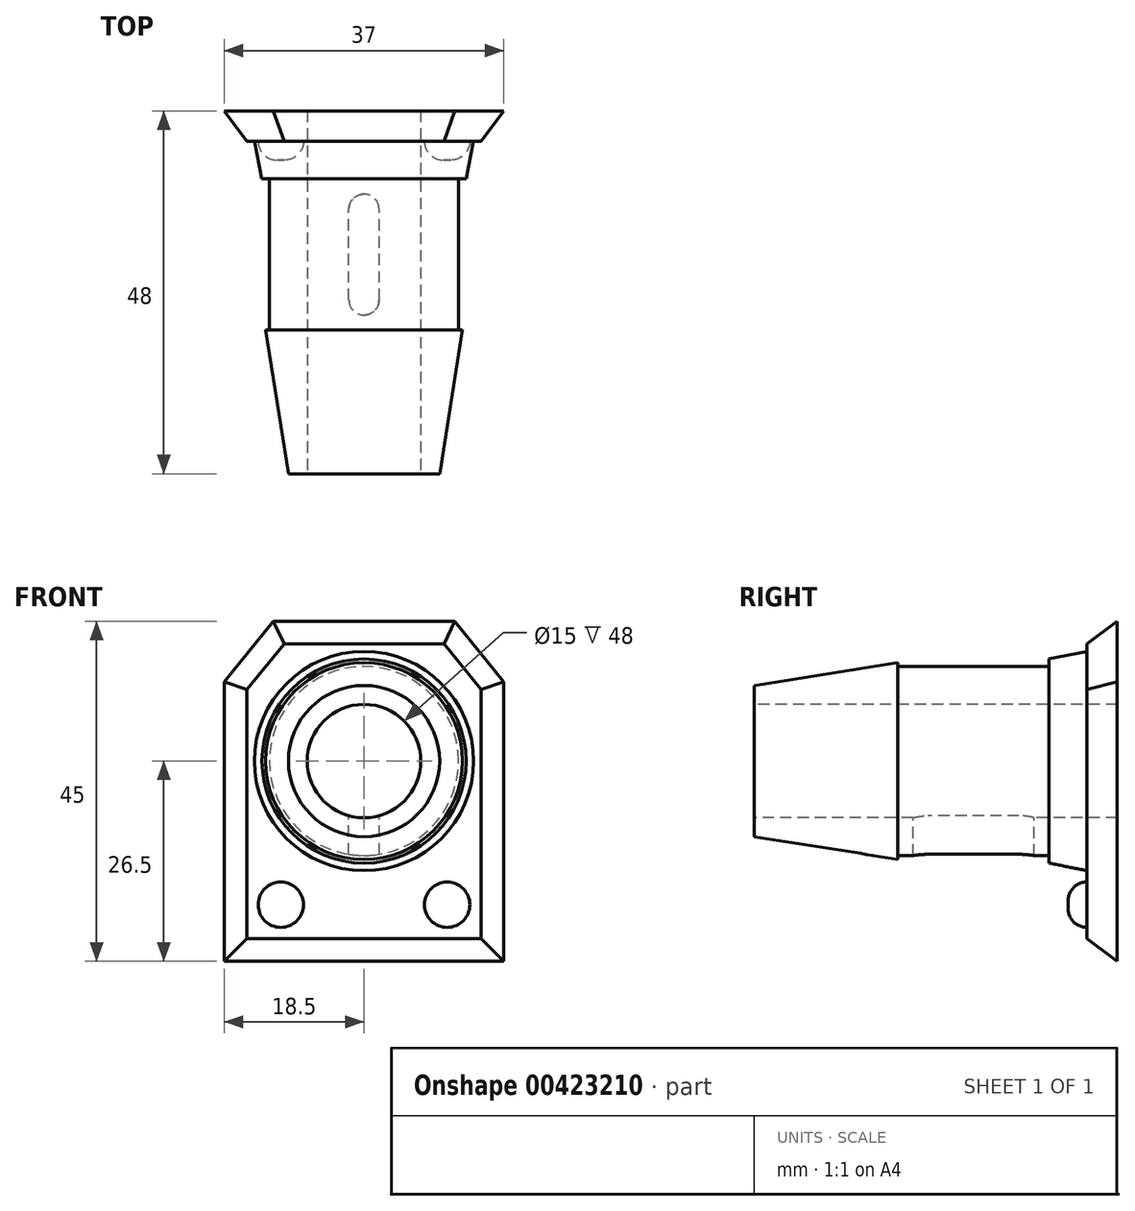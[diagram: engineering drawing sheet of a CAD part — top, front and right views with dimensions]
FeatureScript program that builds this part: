
annotation { "Feature Type Name" : "Feature", "Feature Type Description" : "" }
export const myFeature = defineFeature(function(context is Context, id is Id, definition is map)
    precondition{}
    {
        {
            var Q0;
            Q0=qCreatedBy(makeId("Front.planeOp"),FACE);
            var sketch = newSketch(context, id + "F0", { "sketchPlane" : qUnion([Q0])});
            skLineSegment(sketch, "E0.bottom", {"start": v(-18.5, 22.5) * mm, "end": v(18.5, 22.5) * mm});
            skLineSegment(sketch, "E0.top", {"start": v(-18.5, -22.5) * mm, "end": v(18.5, -22.5) * mm});
            skLineSegment(sketch, "E0.left", {"start": v(-18.5, 22.5) * mm, "end": v(-18.5, -22.5) * mm});
            skLineSegment(sketch, "E0.right", {"start": v(18.5, 22.5) * mm, "end": v(18.5, -22.5) * mm});
            skLineSegment(sketch, "E1", {"start": v(-18.5, 0) * mm, "end": v(18.5, 0) * mm});
            skPoint(sketch, "E2", {"position": v(0, 0) * mm});
            skSolve(sketch);
        }
        {
            var Q0;
            Q0=makeQuery(id+"F0.imprint","IMPRINT",FACE,{"disambiguationData":[TD([[makeQuery(id+"F0.imprint","IMPRINT",EDGE,{"derivedFrom":sQuery(id+"F0.wireOp",EDGE,"E0.bottom")}),-1.0]])]});
            var Q1;
            {var subQ0=sQuery(id+"F0.wireOp",EDGE,"E0.top");Q1=makeQuery(id+"F0.imprint","IMPRINT",FACE,{"disambiguationData":[TD([[makeQuery(id+"F0.imprint","IMPRINT",EDGE,{"derivedFrom":subQ0}),1.0]])]});}
            extrude(context, id + "F1", {"entities" : qUnion([Q0, Q1]), "depth" : 4 * mm});
        }
        {
            var Q0;
            Q0=makeQuery(id+"F1.opExtrude","SWEPT_EDGE",EDGE,{"disambiguationData":[OSD([sQuery(id+"F0.wireOp",EDGE,"E0.bottom"),sQuery(id+"F0.wireOp",EDGE,"E0.left")])]});
            var Q1;
            Q1=makeQuery(id+"F1.opExtrude","SWEPT_EDGE",EDGE,{"disambiguationData":[OSD([sQuery(id+"F0.wireOp",EDGE,"E0.bottom"),sQuery(id+"F0.wireOp",EDGE,"E0.right")])]});
            chamfer(context, id + "F2", {"entities" : qUnion([Q0, Q1]), "chamferType" : ChamferType.TWO_OFFSETS, "width1" : 8 * mm, "oppositeDirection" : false, "width2" : 6.5 * mm, "tangentPropagation" : true});
        }
        {
            var Q0;
            Q0=makeQuery(id+"F1.opExtrude","CAP_EDGE",EDGE,{"disambiguationData":[OSD([sQuery(id+"F0.wireOp",EDGE,"E0.left")])],"isStart":false});
            var Q1;
            Q1=makeQuery(id+"F1.opExtrude","CAP_EDGE",EDGE,{"disambiguationData":[OSD([sQuery(id+"F0.wireOp",EDGE,"E0.top")])],"isStart":false});
            var Q2;
            Q2=makeQuery(id+"F1.opExtrude","CAP_EDGE",EDGE,{"disambiguationData":[OSD([sQuery(id+"F0.wireOp",EDGE,"E0.right")])],"isStart":false});
            var Q3;
            {var subQ0=sQuery(id+"F0.wireOp",EDGE,"E0.right");var subQ1=sQuery(id+"F0.wireOp",EDGE,"E0.bottom");Q3=makeQuery(id+"F2.opChamfer","BLEND_EDGE",EDGE,{"blendedFrom":[makeQuery(id+"F1.opExtrude","SWEPT_EDGE",EDGE,{"disambiguationData":[OSD([subQ1,subQ0])]}),makeQuery(id+"F1.opExtrude","CAP_FACE",FACE,{"disambiguationData":[OSD([subQ1,sQuery(id+"F0.wireOp",EDGE,"E0.top"),sQuery(id+"F0.wireOp",EDGE,"E0.left"),subQ0])],"isStart":false})],"blendedInto":[makeQuery(id+"F1.opExtrude","CAP_FACE",FACE,{"disambiguationData":[OSD([subQ1,sQuery(id+"F0.wireOp",EDGE,"E0.top"),sQuery(id+"F0.wireOp",EDGE,"E0.left"),subQ0])],"isStart":false})]});}
            var Q4;
            {var subQ0=sQuery(id+"F0.wireOp",EDGE,"E0.left");var subQ1=sQuery(id+"F0.wireOp",EDGE,"E0.bottom");Q4=makeQuery(id+"F2.opChamfer","BLEND_EDGE",EDGE,{"blendedFrom":[makeQuery(id+"F1.opExtrude","SWEPT_EDGE",EDGE,{"disambiguationData":[OSD([subQ1,subQ0])]}),makeQuery(id+"F1.opExtrude","CAP_FACE",FACE,{"disambiguationData":[OSD([subQ1,sQuery(id+"F0.wireOp",EDGE,"E0.top"),subQ0,sQuery(id+"F0.wireOp",EDGE,"E0.right")])],"isStart":false})],"blendedInto":[makeQuery(id+"F1.opExtrude","CAP_FACE",FACE,{"disambiguationData":[OSD([subQ1,sQuery(id+"F0.wireOp",EDGE,"E0.top"),subQ0,sQuery(id+"F0.wireOp",EDGE,"E0.right")])],"isStart":false})]});}
            var Q5;
            Q5=makeQuery(id+"F1.opExtrude","CAP_EDGE",EDGE,{"disambiguationData":[OSD([sQuery(id+"F0.wireOp",EDGE,"E0.bottom")])],"isStart":false});
            chamfer(context, id + "F3", {"entities" : qUnion([Q0, Q1, Q2, Q3, Q4, Q5]), "chamferType" : ChamferType.TWO_OFFSETS, "width1" : 3 * mm, "oppositeDirection" : false, "width2" : 4 * mm, "tangentPropagation" : true});
        }
        {
            var Q0;
            Q0=makeQuery(id+"F1.opExtrude","CAP_FACE",FACE,{"disambiguationData":[OSD([sQuery(id+"F0.wireOp",EDGE,"E0.bottom"),sQuery(id+"F0.wireOp",EDGE,"E0.top"),sQuery(id+"F0.wireOp",EDGE,"E0.left"),sQuery(id+"F0.wireOp",EDGE,"E0.right")])],"isStart":false});
            var sketch = newSketch(context, id + "F4", { "sketchPlane" : qUnion([Q0])});
            skLineSegment(sketch, "E3", {"start": v(0, 19.5) * mm, "end": v(0, 4) * mm});
            skCircle(sketch, "E4", {"center": v(0, 4) * mm, "radius": 14.5 * mm});
            skSolve(sketch);
        }
        {
            var Q0;
            Q0=makeQuery(id+"F4.imprint","IMPRINT",FACE,{"disambiguationData":[TD([[makeQuery(id+"F4.imprint","IMPRINT",EDGE,{"derivedFrom":sQuery(id+"F4.wireOp",EDGE,"E4")}),1.0]])]});
            extrude(context, id + "F5", {"entities" : qUnion([Q0]), "operationType" : NewBodyOperationType.ADD, "depth" : 5 * mm});
        }
        {
            var Q0;
            Q0=makeQuery(id+"F5.opExtrude","CAP_FACE",FACE,{"disambiguationData":[OSD([sQuery(id+"F4.wireOp",EDGE,"E4")])],"isStart":false});
            var sketch = newSketch(context, id + "F6", { "sketchPlane" : qUnion([Q0])});
            skCircle(sketch, "E5", {"center": v(0, 4) * mm, "radius": 12.5 * mm});
            skSolve(sketch);
        }
        {
            var Q0;
            Q0=makeQuery(id+"F6.imprint","IMPRINT",FACE,{"disambiguationData":[TD([[makeQuery(id+"F6.imprint","IMPRINT",EDGE,{"derivedFrom":sQuery(id+"F6.wireOp",EDGE,"E5")}),1.0]])]});
            extrude(context, id + "F7", {"entities" : qUnion([Q0]), "operationType" : NewBodyOperationType.ADD, "depth" : 20 * mm});
        }
        {
            var Q0;
            Q0=makeQuery(id+"F7.opExtrude","CAP_FACE",FACE,{"disambiguationData":[OSD([sQuery(id+"F6.wireOp",EDGE,"E5")])],"isStart":false});
            var sketch = newSketch(context, id + "F8", { "sketchPlane" : qUnion([Q0])});
            skCircle(sketch, "E6", {"center": v(0, 4) * mm, "radius": 13 * mm});
            skSolve(sketch);
        }
        {
            var Q0;
            Q0 = qSketchRegion(id + "F8", true);
            extrude(context, id + "F9", {"entities" : qUnion([Q0]), "operationType" : NewBodyOperationType.ADD, "depth" : 19 * mm});
        }
        {
            var Q0;
            Q0=makeQuery(id+"F9.opExtrude","CAP_EDGE",EDGE,{"disambiguationData":[OSD([sQuery(id+"F8.wireOp",EDGE,"E6")])],"isStart":false});
            chamfer(context, id + "F10", {"entities" : qUnion([Q0]), "chamferType" : ChamferType.TWO_OFFSETS, "width1" : 3 * mm, "oppositeDirection" : false, "width2" : 19 * mm, "tangentPropagation" : true});
        }
        {
            var Q0;
            Q0=makeQuery(id+"F9.opExtrude","CAP_FACE",FACE,{"disambiguationData":[OSD([sQuery(id+"F8.wireOp",EDGE,"E6")])],"isStart":false});
            var sketch = newSketch(context, id + "F11", { "sketchPlane" : qUnion([Q0])});
            skCircle(sketch, "E7", {"center": v(0, 4) * mm, "radius": 7.5 * mm});
            skSolve(sketch);
        }
        {
            var Q0;
            Q0 = qSketchRegion(id + "F11", true);
            extrude(context, id + "F12", {"entities" : qUnion([Q0]), "operationType" : NewBodyOperationType.REMOVE, "oppositeDirection" : true, "depth" : 50 * mm});
        }
        {
            var Q0;
            Q0=qCreatedBy(makeId("Top.planeOp"),FACE);
            var sketch = newSketch(context, id + "F13", { "sketchPlane" : qUnion([Q0])});
            skLineSegment(sketch, "E8", {"start": v(0, 0) * mm, "end": v(0, -19) * mm});
            skPoint(sketch, "E9.middle", {"position": v(0, -19) * mm});
            skCircle(sketch, "E10", {"center": v(0, -13) * mm, "radius": 2 * mm});
            skPoint(sketch, "E10.first.point", {"position": v(0, -11) * mm});
            skPoint(sketch, "E10.third.point", {"position": v(-2, -13) * mm});
            skCircle(sketch, "E11", {"center": v(0, -25) * mm, "radius": 2 * mm});
            skPoint(sketch, "E11.second.point", {"position": v(0, -27) * mm});
            skPoint(sketch, "E11.third.point", {"position": v(-2, -25) * mm});
            skLineSegment(sketch, "E12", {"start": v(-2, -13) * mm, "end": v(-2, -25) * mm});
            skLineSegment(sketch, "E13", {"start": v(2, -13) * mm, "end": v(2, -25) * mm});
            skSolve(sketch);
        }
        {
            var Q0;
            Q0 = qSketchRegion(id + "F13", true);
            extrude(context, id + "F14", {"entities" : qUnion([Q0]), "operationType" : NewBodyOperationType.REMOVE, "oppositeDirection" : true, "depth" : 25 * mm});
        }
        {
            var Q0;
            Q0=makeQuery(id+"F5.opExtrude","CAP_EDGE",EDGE,{"disambiguationData":[OSD([sQuery(id+"F4.wireOp",EDGE,"E4")])],"isStart":false});
            chamfer(context, id + "F15", {"entities" : qUnion([Q0]), "chamferType" : ChamferType.TWO_OFFSETS, "width1" : 1 * mm, "oppositeDirection" : false, "width2" : 5 * mm, "tangentPropagation" : true});
        }
        {
            var Q0;
            Q0=makeQuery(id+"F1.opExtrude","CAP_FACE",FACE,{"disambiguationData":[OSD([sQuery(id+"F0.wireOp",EDGE,"E0.bottom"),sQuery(id+"F0.wireOp",EDGE,"E0.top"),sQuery(id+"F0.wireOp",EDGE,"E0.left"),sQuery(id+"F0.wireOp",EDGE,"E0.right")])],"isStart":false});
            var sketch = newSketch(context, id + "F16", { "sketchPlane" : qUnion([Q0])});
            skLineSegment(sketch, "E14", {"start": v(-15.5, -15) * mm, "end": v(-11, -15) * mm});
            skLineSegment(sketch, "E15", {"start": v(-11, -15) * mm, "end": v(-11, -19.5) * mm});
            skCircle(sketch, "E16", {"center": v(-11, -15) * mm, "radius": 3 * mm});
            skLineSegment(sketch, "E17", {"start": v(15.5, -15) * mm, "end": v(11, -15) * mm});
            skCircle(sketch, "E18", {"center": v(11, -15) * mm, "radius": 3 * mm});
            skSolve(sketch);
        }
        {
            var Q0;
            Q0 = qSketchRegion(id + "F16", true);
            extrude(context, id + "F17", {"entities" : qUnion([Q0]), "operationType" : NewBodyOperationType.ADD, "depth" : 2.5 * mm});
        }
        {
            var Q0;
            Q0=makeQuery(id+"F17.opExtrude","CAP_EDGE",EDGE,{"disambiguationData":[OSD([sQuery(id+"F16.wireOp",EDGE,"E18")])],"isStart":false});
            var Q1;
            Q1=makeQuery(id+"F17.opExtrude","CAP_EDGE",EDGE,{"disambiguationData":[OSD([sQuery(id+"F16.wireOp",EDGE,"E16")])],"isStart":false});
            fillet(context, id + "F18", {"entities" : qUnion([Q0, Q1]), "radius" : 2.5 * mm, "tangentPropagation" : true, "allowEdgeOverflow" : false});
        }
    });
